# Revit family: F010-21x24x18
name_source: partatom
category: Furniture Systems
units: mm (PartAtom-declared; Revit-internal decimal feet)

## family parameters
Always vertical = Yes
Cut with Voids When Loaded = No
Part Type = Normal
Room Calculation Point = No
Round Connector Dimension = Use Diameter
Shared = No
Work Plane-Based = No

## types (14) — shared parameters
3" Rectangle Leg = <By Category>
6" Rectangle Leg = <By Category>
Base = <By Category>
Description = Benches - Wedge Bench
Glide = <By Category>
Low Profile = Black
Manufacturer = FOMCORE
Mod Leg = <By Category>
Model = F010-21X24X18
Seat Fabric = <By Category>
Side Fabric = <By Category>
TFL Top = <By Category>
Triangle Leg = <By Category>
URL = https://fomcore.com

## per-type parameters (varying)
| type | BASE | G1 | L1 | LEG OPTIONS | Leg Height | M6 | R3 | R6 | T6 | TOP | TOP HEIGHT |
| F010-21X24X18-G1 | Yes | Yes | No | 1 | 0' - 1 1/2" | No | No | No | No | No | 1' - 5 1/2" |
| F010-21X24X18-G1-TFL | Yes | Yes | No | 1 | 0' - 1 1/2" | No | No | No | No | Yes | 1' - 5" |
| F010-21X24X18-L1 | Yes | No | Yes | 2 | 0' - 1 1/2" | No | No | No | No | No | 1' - 5 1/2" |
| F010-21X24X18-L1-TFL | Yes | No | Yes | 2 | 0' - 1 1/2" | No | No | No | No | Yes | 1' - 5" |
| F010-21X24X18-M6 | Yes | No | No | 3 | 0' - 6 1/2" | Yes | No | No | No | No | 1' - 5 1/2" |
| F010-21X24X18-M6-TFL | Yes | No | No | 3 | 0' - 6 1/2" | Yes | No | No | No | Yes | 1' - 5" |
| F010-21X24X18-R3 | Yes | No | No | 4 | 0' - 3 1/2" | No | Yes | No | No | No | 1' - 5 1/2" |
| F010-21X24X18-R3-TFL | Yes | No | No | 4 | 0' - 3 1/2" | No | Yes | No | No | Yes | 1' - 5" |
| F010-21X24X18-R6 | Yes | No | No | 5 | 0' - 6 1/2" | No | No | Yes | No | No | 1' - 5 1/2" |
| F010-21X24X18-R6-TFL | Yes | No | No | 5 | 0' - 6 1/2" | No | No | Yes | No | Yes | 1' - 5" |
| F010-21X24X18-T6 | Yes | No | No | 6 | 0' - 6 1/2" | No | No | No | Yes | No | 1' - 5 1/2" |
| F010-21X24X18-T6-TFL | Yes | No | No | 6 | 0' - 6 1/2" | No | No | No | Yes | Yes | 1' - 5" |
| F010-21X24X18-Z | No | No | No | 0 | 0' - 0" | No | No | No | No | No | 1' - 5 1/2" |
| F010-21X24X18-Z-TFL | No | No | No | 0 | 0' - 0" | No | No | No | No | Yes | 1' - 5" |

## geometry (parser evidence)
native form markers: Sweep x2
no freeform markers — native parametric forms only
